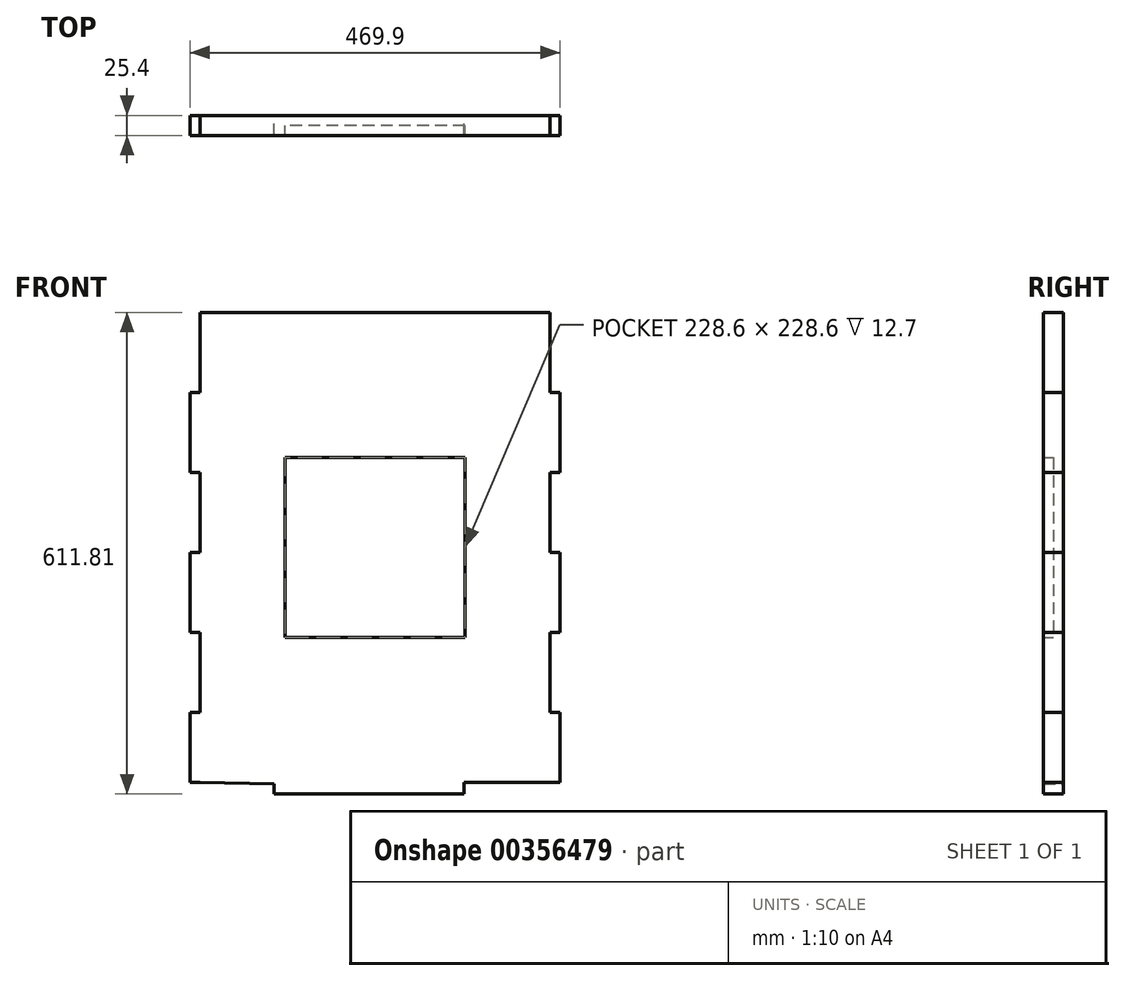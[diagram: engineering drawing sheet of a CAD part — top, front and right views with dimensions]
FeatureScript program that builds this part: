
annotation { "Feature Type Name" : "Feature", "Feature Type Description" : "" }
export const myFeature = defineFeature(function(context is Context, id is Id, definition is map)
    precondition{}
    {
        {
            var Q0;
            Q0=qCreatedBy(makeId("Front.planeOp"),FACE);
            var sketch = newSketch(context, id + "F0", { "sketchPlane" : qUnion([Q0])});
            skLineSegment(sketch, "E0.bottom", {"start": v(-222.25, 298.45) * mm, "end": v(222.25, 298.45) * mm});
            skLineSegment(sketch, "E0.top", {"start": v(-222.25, -298.45) * mm, "end": v(222.25, -298.45) * mm});
            skLineSegment(sketch, "E0.left", {"start": v(-222.25, 298.45) * mm, "end": v(-222.25, -298.45) * mm});
            skLineSegment(sketch, "E0.right", {"start": v(222.25, 298.45) * mm, "end": v(222.25, -298.45) * mm});
            skLineSegment(sketch, "E1.left", {"start": v(222.25, 298.45) * mm, "end": v(222.25, 196.85) * mm});
            skLineSegment(sketch, "E2.bottom", {"start": v(222.25, 196.85) * mm, "end": v(234.95, 196.85) * mm});
            skLineSegment(sketch, "E2.top", {"start": v(222.25, 95.25) * mm, "end": v(234.95, 95.25) * mm});
            skLineSegment(sketch, "E2.left", {"start": v(222.25, 196.85) * mm, "end": v(222.25, 95.25) * mm});
            skLineSegment(sketch, "E2.right", {"start": v(234.95, 196.85) * mm, "end": v(234.95, 95.25) * mm});
            skLineSegment(sketch, "E3", {"start": v(222.25, 95.25) * mm, "end": v(222.25, -6.35) * mm});
            skLineSegment(sketch, "E4.bottom", {"start": v(222.25, -6.35) * mm, "end": v(234.95, -6.35) * mm});
            skLineSegment(sketch, "E4.top", {"start": v(222.25, -107.95) * mm, "end": v(234.95, -107.95) * mm});
            skLineSegment(sketch, "E4.left", {"start": v(222.25, -6.35) * mm, "end": v(222.25, -107.95) * mm});
            skLineSegment(sketch, "E4.right", {"start": v(234.95, -6.35) * mm, "end": v(234.95, -107.95) * mm});
            skLineSegment(sketch, "E5", {"start": v(222.25, -107.95) * mm, "end": v(222.25, -209.55) * mm});
            skLineSegment(sketch, "E6.bottom", {"start": v(222.25, -209.55) * mm, "end": v(234.95, -209.55) * mm});
            skLineSegment(sketch, "E6.top", {"start": v(222.25, -298.45) * mm, "end": v(234.95, -298.45) * mm});
            skLineSegment(sketch, "E6.left", {"start": v(222.25, -209.55) * mm, "end": v(222.25, -298.45) * mm});
            skLineSegment(sketch, "E6.right", {"start": v(234.95, -209.55) * mm, "end": v(234.95, -298.45) * mm});
            skLineSegment(sketch, "E7", {"start": v(0, 298.45) * mm, "end": v(0, -298.45) * mm});
            skLineSegment(sketch, "E8.MirrorCS", {"start": v(-222.25, -298.45) * mm, "end": v(-234.95, -298.45) * mm});
            skLineSegment(sketch, "E9.MirrorCS", {"start": v(-222.25, -209.55) * mm, "end": v(-234.95, -209.55) * mm});
            skLineSegment(sketch, "E10.MirrorCS", {"start": v(-222.25, 196.85) * mm, "end": v(-234.95, 196.85) * mm});
            skLineSegment(sketch, "E11.MirrorCS", {"start": v(-222.25, -107.95) * mm, "end": v(-234.95, -107.95) * mm});
            skLineSegment(sketch, "E12.MirrorCS", {"start": v(-222.25, 95.25) * mm, "end": v(-234.95, 95.25) * mm});
            skLineSegment(sketch, "E13.MirrorCS", {"start": v(-222.25, -6.35) * mm, "end": v(-234.95, -6.35) * mm});
            skLineSegment(sketch, "E14.MirrorCS", {"start": v(-222.25, -107.95) * mm, "end": v(-222.25, -209.55) * mm});
            skLineSegment(sketch, "E15.MirrorCS", {"start": v(-222.25, -209.55) * mm, "end": v(-222.25, -298.45) * mm});
            skLineSegment(sketch, "E16.MirrorCS", {"start": v(-234.95, -209.55) * mm, "end": v(-234.95, -298.45) * mm});
            skLineSegment(sketch, "E17.MirrorCS", {"start": v(222.25, 298.45) * mm, "end": v(-222.25, 298.45) * mm});
            skLineSegment(sketch, "E18.MirrorCS", {"start": v(-234.95, -6.35) * mm, "end": v(-234.95, -107.95) * mm});
            skLineSegment(sketch, "E19.MirrorCS", {"start": v(-222.25, 95.25) * mm, "end": v(-222.25, -6.35) * mm});
            skLineSegment(sketch, "E20.MirrorCS", {"start": v(-234.95, 196.85) * mm, "end": v(-234.95, 95.25) * mm});
            skLineSegment(sketch, "E21.MirrorCS", {"start": v(-222.25, 196.85) * mm, "end": v(-222.25, 95.25) * mm});
            skLineSegment(sketch, "E22.MirrorCS", {"start": v(-222.25, 298.45) * mm, "end": v(-222.25, 196.85) * mm});
            skLineSegment(sketch, "E23.MirrorCS", {"start": v(-222.25, -6.35) * mm, "end": v(-222.25, -107.95) * mm});
            skLineSegment(sketch, "E24.MirrorCS", {"start": v(222.25, -298.45) * mm, "end": v(-222.25, -298.45) * mm});
            skLineSegment(sketch, "E25.bottom", {"start": v(-222.25, -298.45) * mm, "end": v(-128.23, -300.66) * mm});
            skLineSegment(sketch, "E25.right", {"start": v(-128.23, -300.66) * mm, "end": v(-128.23, -313.36) * mm});
            skLineSegment(sketch, "E26", {"start": v(-128.23, -313.36) * mm, "end": v(113.07, -313.36) * mm});
            skLineSegment(sketch, "E27", {"start": v(113.07, -313.36) * mm, "end": v(113.07, -298.45) * mm});
            skLineSegment(sketch, "E28.bottom", {"start": v(114.3, 114.3) * mm, "end": v(-114.3, 114.3) * mm});
            skLineSegment(sketch, "E28.top", {"start": v(114.3, -114.3) * mm, "end": v(-114.3, -114.3) * mm});
            skLineSegment(sketch, "E28.left", {"start": v(114.3, 114.3) * mm, "end": v(114.3, -114.3) * mm});
            skLineSegment(sketch, "E28.right", {"start": v(-114.3, 114.3) * mm, "end": v(-114.3, -114.3) * mm});
            skPoint(sketch, "E28.middle", {"position": v(0, 0) * mm});
            skSolve(sketch);
        }
        {
            var Q0;
            Q0 = qSketchRegion(id + "F0", true);
            extrude(context, id + "F1", {"entities" : qUnion([Q0]), "depth" : 25.4 * mm});
        }
        {
            var Q0;
            {var subQ5=sQuery(id+"F0.wireOp",EDGE,"E28.right");Q0=makeQuery(id+"F0.imprint","IMPRINT",FACE,{"disambiguationData":[TD([[makeQuery(id+"F0.imprint","IMPRINT",EDGE,{"derivedFrom":subQ5}),1.0]])]});}
            var Q1;
            {var subQ5=sQuery(id+"F0.wireOp",EDGE,"E28.left");Q1=makeQuery(id+"F0.imprint","IMPRINT",FACE,{"disambiguationData":[TD([[makeQuery(id+"F0.imprint","IMPRINT",EDGE,{"derivedFrom":subQ5}),-1.0]])]});}
            extrude(context, id + "F2", {"entities" : qUnion([Q0, Q1]), "operationType" : NewBodyOperationType.ADD, "depth" : 12.7 * mm});
        }
    });
